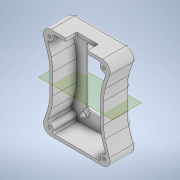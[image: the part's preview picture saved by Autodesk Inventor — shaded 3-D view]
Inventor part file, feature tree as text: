
AUTODESK INVENTOR PART (.ipt)
format: ipt  version: 2021 (Build 250183000, 183)  size: 387,584 bytes
history: native  units: mm
features: extrude x9, sketch x9, mirror x8, fillet x7, shell x1, plane x1
ambient origin geometry x8: Origin, YZ Plane, XZ Plane, XY Plane, X Axis, Y Axis, Z Axis, Center Point
bodies: Solid1 (feature_tree)
feature tree (35):
  extrude  "Extrusion1"  Depth=60.0mm
  extrude  "Extrusion2"  Depth=7.0mm
  mirror  "Mirror1"
  mirror  "Mirror2"
  fillet  "Fillet2"  Radius=20.0mm
  fillet  "Fillet3"  Radius=75.0mm
  shell  "Shell2"  Thickness=16.75mm
  extrude  "Extrusion3"  Depth=30.0mm
  fillet  "Fillet4"  Radius=5.0mm
  extrude  "Extrusion4"  Depth=2.0mm
  mirror  "Mirror4"
  mirror  "Mirror5"
  fillet  "Fillet5"  Radius=18.0mm
  plane  "Work Plane1"
  extrude  "Extrusion5"  Depth=1.0mm
  fillet  "Fillet6"  Radius=2.5mm
  mirror  "Mirror6"
  extrude  "Extrusion6"  Depth=5.0mm
  fillet  "Fillet7"  Radius=5.0mm
  mirror  "Mirror7"
  extrude  "Extrusion7"  Depth=1.0mm
  mirror  "Mirror8"
  extrude  "Extrusion8"  Depth=8.89mm
  mirror  "Mirror9"
  extrude  "Extrusion9"  Depth=0.5mm TaperAngle=0.0deg
  fillet  "Fillet8"  Radius=0.5mm
  sketch  "Sketch1"  dims[d0=35.0mm d1=60.0mm]
  sketch  "Sketch2"  dims[d2=17.25mm d3=0.0mm d5=7.0mm d7=20.0mm d8=75.0mm d9=16.75mm d10=0.0mm]
  sketch  "Sketch3"  dims[d12=2.0mm d13=30.0mm d14=5.0mm]
  sketch  "Sketch4"  dims[d15=2.0mm d16=38.0mm d17=18.0mm]
  sketch  "Sketch5"  dims[d18=0.0mm d19=0.0mm d20=1.0mm d21=2.5mm]
  sketch  "Sketch6"  dims[d22=1.0mm d23=1.9mm d24=5.0mm]
  sketch  "Sketch7"  dims[d25=0.0mm d26=0.0mm d27=1.0mm]
  sketch  "Sketch8"  dims[d28=20.86mm d29=8.89mm]
  sketch  "Sketch9"  dims[d30=3.6mm d31=1.5mm d32=0.0mm d33=0.5mm d34=24.86mm d35=8.89mm d36=1.5mm d37=0.0mm d38=0.5mm d39=1.75mm d40=2.0mm d41=0.0mm d42=1.9mm d43=2.0mm d44=0.0mm d45=7.0mm d46=14.0mm d47=2.0mm d48=0.0mm d49=0.5mm]
